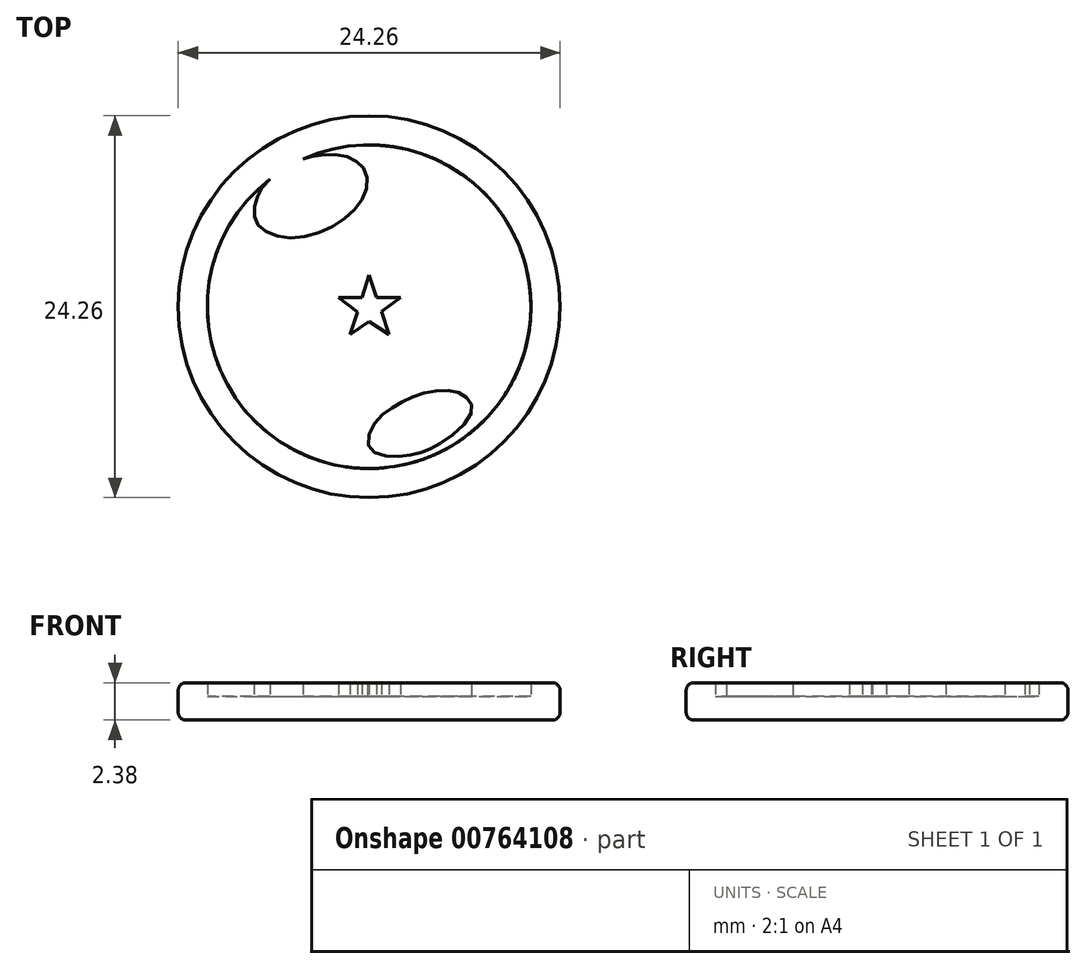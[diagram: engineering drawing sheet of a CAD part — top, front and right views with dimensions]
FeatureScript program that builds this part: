
annotation { "Feature Type Name" : "Feature", "Feature Type Description" : "" }
export const myFeature = defineFeature(function(context is Context, id is Id, definition is map)
    precondition{}
    {
        {
            var Q0;
            Q0=qCreatedBy(makeId("Top.planeOp"),FACE);
            var sketch = newSketch(context, id + "F0", { "sketchPlane" : qUnion([Q0])});
            skCircle(sketch, "E0", {"center": v(0, 0) * mm, "radius": 12.12 * mm});
            skCircle(sketch, "E1", {"center": v(0, 0) * mm, "radius": 10.28 * mm});
            skLineSegment(sketch, "E2", {"start": v(-1.96, 0.58) * mm, "end": v(-0.45, 0.58) * mm});
            skLineSegment(sketch, "E3", {"start": v(-0.45, 0.58) * mm, "end": v(0, 2.02) * mm});
            skLineSegment(sketch, "E4", {"start": v(0, 2.02) * mm, "end": v(0.48, 0.58) * mm});
            skLineSegment(sketch, "E5", {"start": v(0.48, 0.58) * mm, "end": v(1.98, 0.58) * mm});
            skLineSegment(sketch, "E6", {"start": v(1.98, 0.58) * mm, "end": v(0.8, -0.3) * mm});
            skLineSegment(sketch, "E7", {"start": v(0.8, -0.3) * mm, "end": v(1.25, -1.76) * mm});
            skLineSegment(sketch, "E8", {"start": v(1.25, -1.76) * mm, "end": v(0, -0.93) * mm});
            skLineSegment(sketch, "E9", {"start": v(0, -0.93) * mm, "end": v(-1.2, -1.76) * mm});
            skLineSegment(sketch, "E10", {"start": v(-1.2, -1.76) * mm, "end": v(-0.75, -0.35) * mm});
            skLineSegment(sketch, "E11", {"start": v(-0.75, -0.35) * mm, "end": v(-1.96, 0.58) * mm});
            skFitSpline(sketch, "E12", {"points": [v(-6.3, 8.11) * mm, v(-7.01, 7.2) * mm, v(-7.3, 6.15) * mm, v(-7.13, 5.32) * mm, v(-6.26, 4.62) * mm, v(-4.62, 4.38) * mm, v(-2.54, 5) * mm, v(-0.97, 6.15) * mm, v(-0.2, 7.36) * mm, v(-0.21, 8.51) * mm, v(-0.82, 9.24) * mm, v(-1.95, 9.66) * mm, v(-3.54, 9.55) * mm, v(-4.2, 9.38) * mm, v(-6.3, 8.11) * mm]});
            skFitSpline(sketch, "E13", {"points": [v(4.51, -8.7) * mm, v(3.2, -9.27) * mm, v(1.39, -9.51) * mm, v(0, -8.91) * mm, v(0.35, -7.4) * mm, v(1.75, -6.24) * mm, v(3.36, -5.52) * mm, v(5.23, -5.36) * mm, v(6.3, -5.86) * mm, v(6.46, -6.82) * mm, v(4.51, -8.7) * mm]});
            skSolve(sketch);
        }
        {
            assignVariable(context, id + "F1", {"name" : "ESTR", "anyValue" : 2.38});
        }
        {
            var Q0;
            Q0=makeQuery(id+"F0.imprint","IMPRINT",FACE,{"disambiguationData":[TD([[makeQuery(id+"F0.imprint","IMPRINT",EDGE,{"derivedFrom":sQuery(id+"F0.wireOp",EDGE,"E0")}),1.0]])]});
            extrude(context, id + "F2", {"entities" : qUnion([Q0]), "depth" : (getVariable(context, 'ESTR')) * mm, "offsetDistance" : 25 * mm});
        }
        {
            var Q0;
            Q0=makeQuery(id+"F2.opExtrude","CAP_EDGE",EDGE,{"disambiguationData":[OSD([sQuery(id+"F0.wireOp",EDGE,"E0")])],"isStart":false});
            var Q1;
            Q1=makeQuery(id+"F2.opExtrude","CAP_EDGE",EDGE,{"disambiguationData":[OSD([sQuery(id+"F0.wireOp",EDGE,"E0")])],"isStart":true});
            fillet(context, id + "F3", {"entities" : qUnion([Q0, Q1]), "radius" : 0.5 * mm, "tangentPropagation" : true, "allowEdgeOverflow" : false});
        }
        {
            var Q0;
            {var subQ0=sQuery(id+"F0.wireOp",EDGE,"E12");var subQ1=sQuery(id+"F0.wireOp",EDGE,"E1");var subQ2=makeQuery(id+"F0.imprint","INTERSECT",VERTEX,{"disambiguationData":[OD(0.0)],"derivedFrom":[subQ1,subQ0]});Q0=makeQuery(id+"F0.imprint","IMPRINT",FACE,{"disambiguationData":[TD([[makeQuery(id+"F0.imprint","IMPRINT",EDGE,{"disambiguationData":[TD([[subQ2,1.0]])],"derivedFrom":subQ1}),1.0]])]});}
            var Q1;
            Q1=makeQuery(id+"F0.imprint","IMPRINT",FACE,{"disambiguationData":[TD([[makeQuery(id+"F0.imprint","IMPRINT",EDGE,{"derivedFrom":sQuery(id+"F0.wireOp",EDGE,"E2")}),1.0]])]});
            var Q2;
            Q2=makeQuery(id+"F0.imprint","IMPRINT",FACE,{"disambiguationData":[TD([[makeQuery(id+"F0.imprint","IMPRINT",EDGE,{"derivedFrom":sQuery(id+"F0.wireOp",EDGE,"E13")}),-1.0]])]});
            var Q3;
            Q3=makeQuery(id+"F0.imprint","IMPRINT",FACE,{"disambiguationData":[TD([[makeQuery(id+"F0.imprint","IMPRINT",EDGE,{"derivedFrom":sQuery(id+"F0.wireOp",EDGE,"E2")}),-1.0]])]});
            extrude(context, id + "F4", {"entities" : qUnion([Q0, Q1, Q2, Q3]), "operationType" : NewBodyOperationType.ADD, "depth" : 1.5 * mm, "offsetDistance" : 25 * mm});
        }
        {
            var Q0;
            {var subQ0=sQuery(id+"F0.wireOp",EDGE,"E12");var subQ1=sQuery(id+"F0.wireOp",EDGE,"E1");var subQ2=makeQuery(id+"F0.imprint","INTERSECT",VERTEX,{"disambiguationData":[OD(0.0)],"derivedFrom":[subQ1,subQ0]});Q0=makeQuery(id+"F0.imprint","IMPRINT",FACE,{"disambiguationData":[TD([[makeQuery(id+"F0.imprint","IMPRINT",EDGE,{"disambiguationData":[TD([[subQ2,1.0]])],"derivedFrom":subQ1}),1.0]])]});}
            var Q1;
            Q1=makeQuery(id+"F0.imprint","IMPRINT",FACE,{"disambiguationData":[TD([[makeQuery(id+"F0.imprint","IMPRINT",EDGE,{"derivedFrom":sQuery(id+"F0.wireOp",EDGE,"E2")}),-1.0]])]});
            var Q2;
            Q2=makeQuery(id+"F0.imprint","IMPRINT",FACE,{"disambiguationData":[TD([[makeQuery(id+"F0.imprint","IMPRINT",EDGE,{"derivedFrom":sQuery(id+"F0.wireOp",EDGE,"E13")}),-1.0]])]});
            var Q3;
            Q3=makeQuery(id+"F2.opExtrude","CAP_FACE",FACE,{"disambiguationData":[OSD([sQuery(id+"F0.wireOp",EDGE,"E0"),sQuery(id+"F0.wireOp",EDGE,"E1"),sQuery(id+"F0.wireOp",EDGE,"E12")])],"isStart":false});
            extrude(context, id + "F5", {"entities" : qUnion([Q0, Q1, Q2]), "operationType" : NewBodyOperationType.ADD, "endBound" : BoundingType.UP_TO_SURFACE, "depth" : 2 * mm, "endBoundEntityFace" : qUnion([Q3]), "offsetDistance" : 25 * mm});
        }
    });
